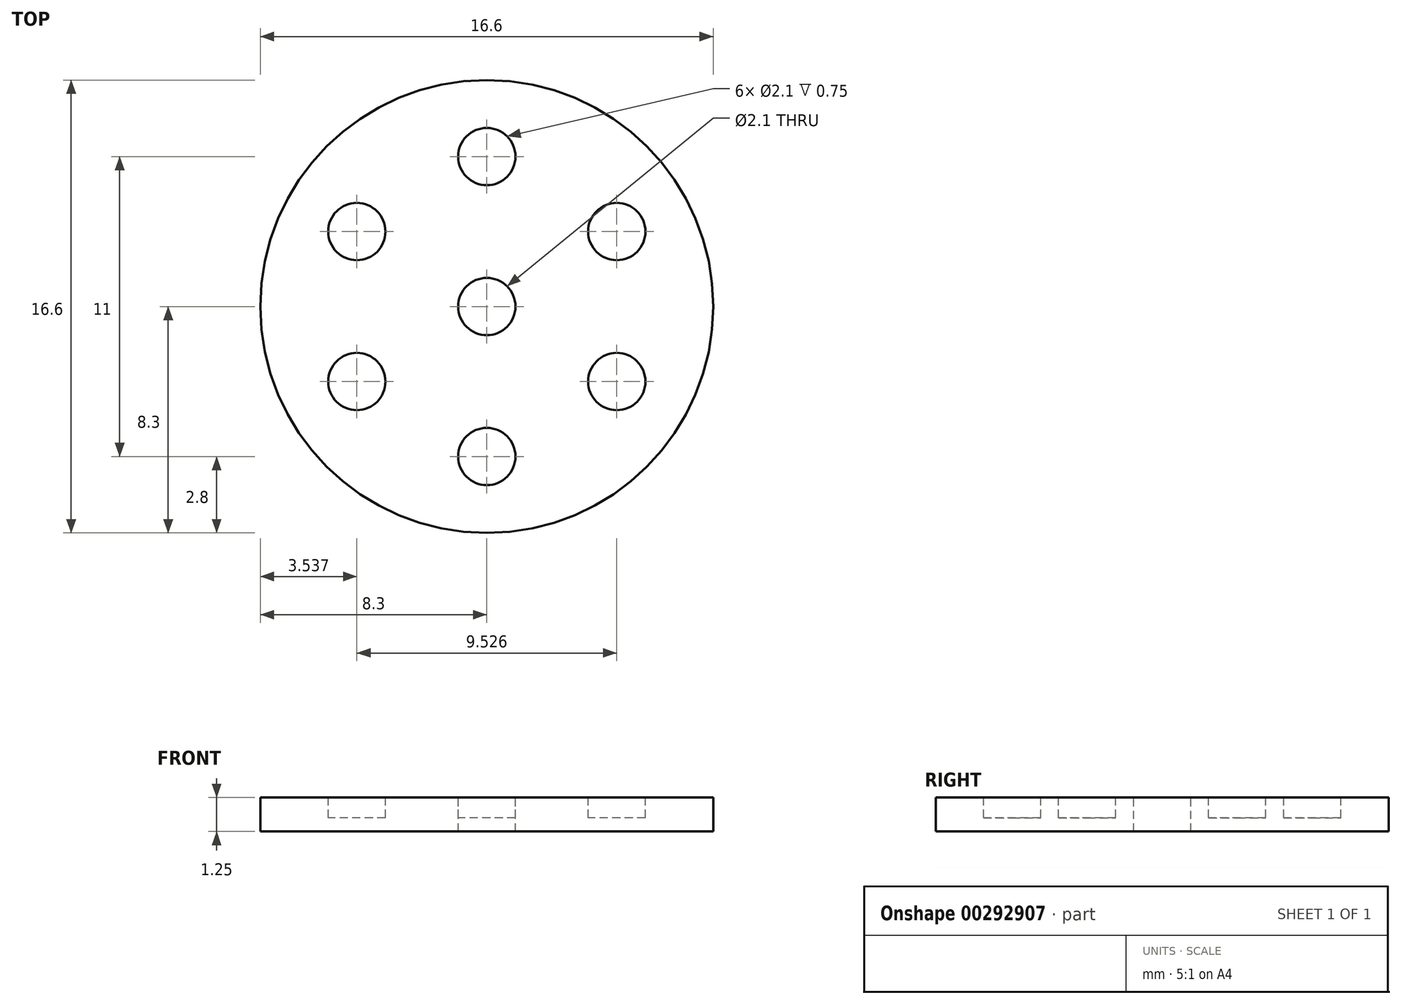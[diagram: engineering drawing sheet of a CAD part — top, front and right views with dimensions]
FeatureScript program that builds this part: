
annotation { "Feature Type Name" : "Feature", "Feature Type Description" : "" }
export const myFeature = defineFeature(function(context is Context, id is Id, definition is map)
    precondition{}
    {
        {
            var Q0;
            Q0=qCreatedBy(makeId("Top.planeOp"),FACE);
            var sketch = newSketch(context, id + "F0", { "sketchPlane" : qUnion([Q0])});
            skCircle(sketch, "E0", {"center": v(0, 0) * mm, "radius": 8.3 * mm});
            skSolve(sketch);
        }
        {
            var Q0;
            Q0 = qSketchRegion(id + "F0", true);
            extrude(context, id + "F1", {"entities" : qUnion([Q0]), "depth" : 1.25 * mm});
        }
        {
            var Q0;
            Q0=makeQuery(id+"F1.opExtrude","CAP_FACE",FACE,{"disambiguationData":[OSD([sQuery(id+"F0.wireOp",EDGE,"E0")])],"isStart":false});
            var sketch = newSketch(context, id + "F2", { "sketchPlane" : qUnion([Q0])});
            skCircle(sketch, "E1", {"center": v(0, 0) * mm, "radius": 1.05 * mm});
            skSolve(sketch);
        }
        {
            var Q0;
            Q0 = qSketchRegion(id + "F2", true);
            extrude(context, id + "F3", {"entities" : qUnion([Q0]), "operationType" : NewBodyOperationType.REMOVE, "oppositeDirection" : true, "depth" : 25 * mm});
        }
        {
            var Q0;
            Q0=makeQuery(id+"F1.opExtrude","CAP_FACE",FACE,{"disambiguationData":[OSD([sQuery(id+"F0.wireOp",EDGE,"E0")])],"isStart":false});
            var sketch = newSketch(context, id + "F4", { "sketchPlane" : qUnion([Q0])});
            skLineSegment(sketch, "E2", {"start": v(0, 0) * mm, "end": v(0, 5.5) * mm, "construction": true});
            skCircle(sketch, "E3", {"center": v(0, 5.5) * mm, "radius": 1.05 * mm});
            skCircle(sketch, "E4.1.0", {"center": v(-4.76, 2.75) * mm, "radius": 1.05 * mm});
            skCircle(sketch, "E4.2.0", {"center": v(-4.76, -2.75) * mm, "radius": 1.05 * mm});
            skCircle(sketch, "E4.3.0", {"center": v(0, -5.5) * mm, "radius": 1.05 * mm});
            skCircle(sketch, "E4.4.0", {"center": v(4.76, -2.75) * mm, "radius": 1.05 * mm});
            skCircle(sketch, "E4.5.0", {"center": v(4.76, 2.75) * mm, "radius": 1.05 * mm});
            skPoint(sketch, "E4.center", {"position": v(0, 0) * mm});
            skSolve(sketch);
        }
        {
            var Q0;
            Q0 = qSketchRegion(id + "F4", true);
            extrude(context, id + "F5", {"entities" : qUnion([Q0]), "operationType" : NewBodyOperationType.REMOVE, "oppositeDirection" : true, "depth" : 0.75 * mm});
        }
    });
